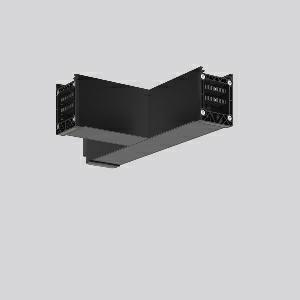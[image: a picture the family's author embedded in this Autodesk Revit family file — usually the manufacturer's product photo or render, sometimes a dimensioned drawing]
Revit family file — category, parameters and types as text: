
# Revit family: linedo_t-verbindung_982774_003_5_b931
name_source: partatom
category: Lighting Fixtures
units: mm (PartAtom-declared; Revit-internal decimal feet)

## family parameters
Cut with Voids When Loaded = No
Host = Face
Light Source = No
Part Type = Normal
Room Calculation Point = No
Round Connector Dimension = Use Diameter
Shared = No

## types (1)
- LINEDO T-Verbindung
    Apparent Load = 0 VA
    Default Elevation = 1800 mm
    Description = Series: LINEDO
T-connector, 7-pole, connection socket / plug - socket. Housing: extruded aluminium profile, powder-coated. Cover made of plastic, surface like housing. LINEDO plug system, plastic, black. Easy connection for rigid or flexible wires. 5 membrane cable entries (2 x M20 and 3 x M25). Suitable for power supply in 7-pole version. Ready prewired. Colour-coded individual cables enable easy electromechanical separation.
Colour: jet black (RAL 9005)
Length: 330 mm
Width: 185 mm
Height: 76 mm
Weight: 940 g
    Height = 76 mm
    Lamp = 0 x
    Length = 331 mm
    Luminous efficacy = 0 lm/W
    Manufacturer = RZB
    ModVariant = No
    Model = 982774.003.5
    Mounting Place = Ceiling
    Mounting Type = Surface mounted
    Number of Poles = 1
    OnlyDefault = Yes
    Power Factor = 1
    Product Name = LINEDO T-Verbindung
    Product group = Surface mounted continuous line luminaire system
    ProductGroupID = 310
    Protection Class = Protection class I
    Protection Degree = Degree of protection
    RLX_Detail_Level = 1
    RLX_Emergency_Light_Flux = 0 lm
    RLX_Emergency_Type = 0
    RLX_Emergency_Type_DB = No
    RlxData = <blob elided: 19873 chars, md5=33c6cc85>
    Standby Power = 0 W
    System Light Flux = 0 lm
    System Power = 0 W
    Type Comments = Product without accessories
    Type Image = 982774.003.1.jpg
    URL = http://relux.com
    VarID = ---
    Voltage = 0 V
    Weight = 0.00 kg
    Width = 185 mm

## geometry (parser evidence)
native form markers: Blend x4, Sweep x11
no freeform markers — native parametric forms only
